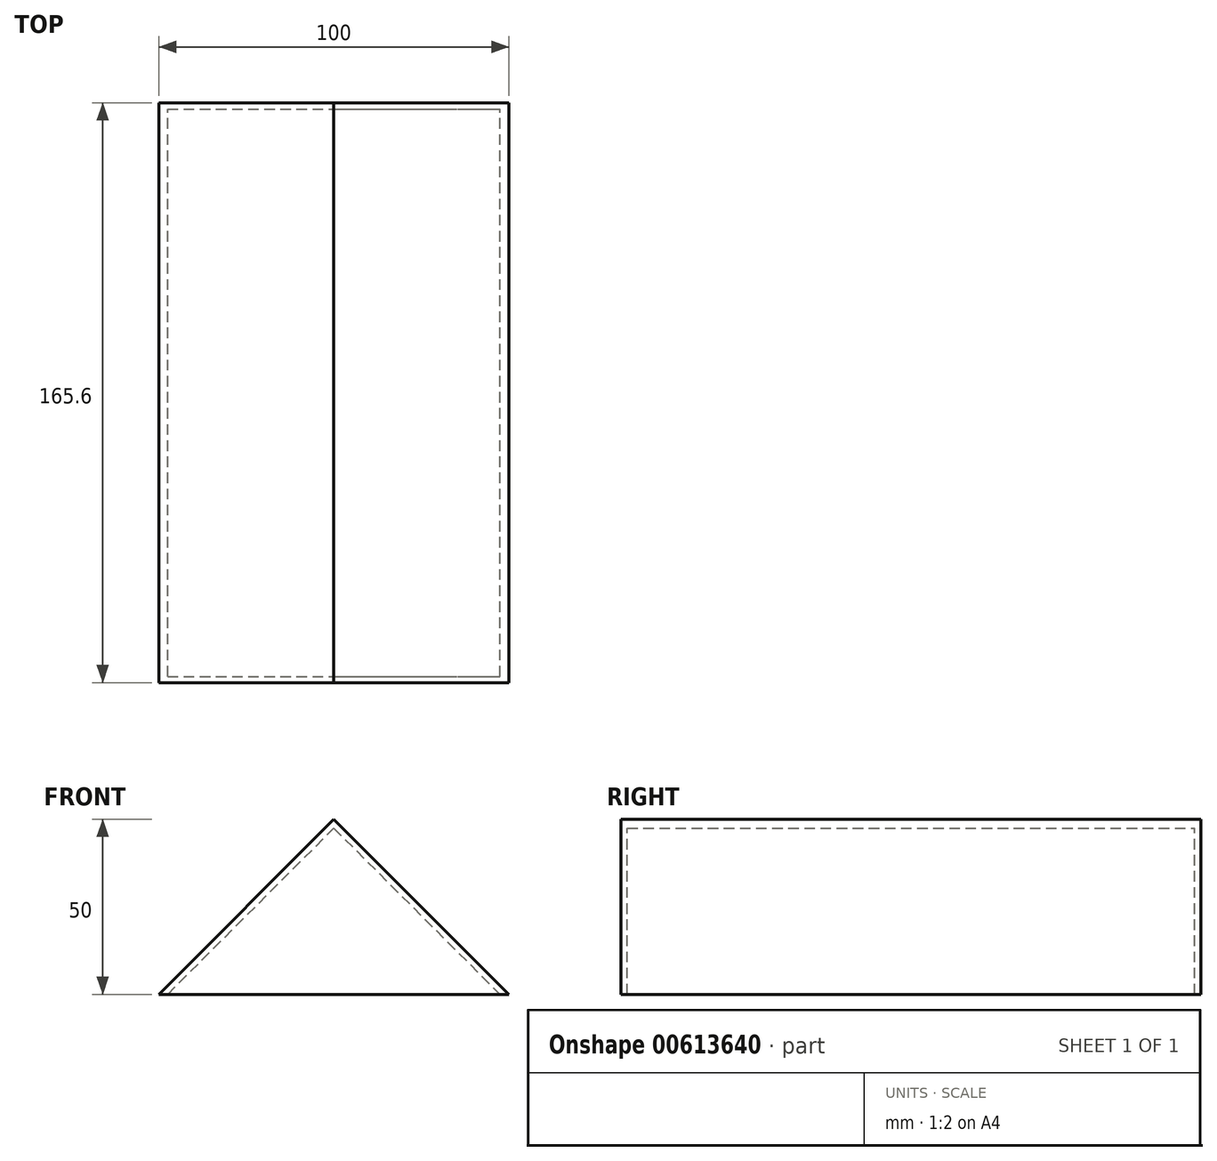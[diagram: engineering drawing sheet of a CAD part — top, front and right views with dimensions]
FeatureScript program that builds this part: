
annotation { "Feature Type Name" : "Feature", "Feature Type Description" : "" }
export const myFeature = defineFeature(function(context is Context, id is Id, definition is map)
    precondition{}
    {
        {
            var Q0;
            Q0=qCreatedBy(makeId("Front.planeOp"),FACE);
            var sketch = newSketch(context, id + "F0", { "sketchPlane" : qUnion([Q0])});
            skLineSegment(sketch, "E0.bottom", {"start": v(-50, 25) * mm, "end": v(50, 25) * mm});
            skLineSegment(sketch, "E0.top", {"start": v(-50, -25) * mm, "end": v(50, -25) * mm});
            skLineSegment(sketch, "E0.left", {"start": v(-50, 25) * mm, "end": v(-50, -25) * mm});
            skLineSegment(sketch, "E0.right", {"start": v(50, 25) * mm, "end": v(50, -25) * mm});
            skPoint(sketch, "E0.middle", {"position": v(0, 0) * mm});
            skLineSegment(sketch, "E1", {"start": v(-50, -25) * mm, "end": v(0, 25) * mm});
            skLineSegment(sketch, "E2", {"start": v(0, 25) * mm, "end": v(50, -25) * mm});
            skSolve(sketch);
        }
        {
            var Q0;
            Q0=makeQuery(id+"F0.imprint","IMPRINT",FACE,{"disambiguationData":[TD([[makeQuery(id+"F0.imprint","IMPRINT",EDGE,{"derivedFrom":sQuery(id+"F0.wireOp",EDGE,"E0.top")}),1.0]])]});
            extrude(context, id + "F1", {"entities" : qUnion([Q0]), "depth" : 165.6 * mm, "offsetDistance" : 25 * mm});
        }
        {
            var Q0;
            Q0=makeQuery(id+"F1.opExtrude","SWEPT_FACE",FACE,{"disambiguationData":[OSD([sQuery(id+"F0.wireOp",EDGE,"E0.top")])]});
            shell(context, id + "F2", {"entities" : qUnion([Q0]), "thickness" : 1.8 * mm});
        }
    });
